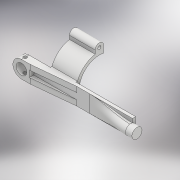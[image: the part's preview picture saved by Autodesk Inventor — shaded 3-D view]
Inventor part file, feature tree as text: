
AUTODESK INVENTOR PART (.ipt)
format: ipt  version: 2018 (Build 220112000, 112)  size: 248,320 bytes
history: native  units: mm
features: sketch x8, extrude x7, plane x3, projected_geometry x2, loft x1, mirror x1
ambient origin geometry x8: Origin, YZ Plane, XZ Plane, XY Plane, X Axis, Y Axis, Z Axis, Center Point
bodies: Solid1 (feature_tree)
feature tree (22):
  sketch  "Sketch1"  dims[d0=10.0mm d2=3.0mm]
  extrude  "Extrusion1"  Depth=3.0mm
  extrude  "Extrusion2"  Depth=16.0mm
  plane  "Work Plane1"
  extrude  "Extrusion3"  Depth=4.0mm TaperAngle=0.0deg
  sketch  "Sketch3"  dims[d5=3.0mm d6=0.0mm d7=4.0mm d8=0.0mm]
  plane  "Work Plane2"
  loft  "Loft1"
  extrude  "Extrusion4"  [1 undecoded]
  extrude  "Extrusion5"  Depth=10.0mm TaperAngle=90.0deg
  mirror  "Mirror1"
  extrude  "Extrusion6"  Depth=5.0mm TaperAngle=0.0deg
  plane  "Work Plane3"
  extrude  "Extrusion13"  Depth=24.0mm
  sketch  "Sketch2"  dims[d3=100.0mm d4=16.0mm]
  projected_geometry  "Projected Loop1"
  sketch  "Sketch4"  dims[d9=6.0mm d10=9.525mm]
  sketch  "Sketch6"  dims[d11=6.0mm d12=0.0mm d13=-40.0mm]
  sketch  "Sketch7"  dims[d14=10.0mm d15=90.0deg d16=10.0mm d17=90.0deg]
  projected_geometry  "Projected Loop2"
  sketch  "Sketch8"  dims[d20=40.0mm d21=5.0mm d22=0.0mm]
  sketch  "Sketch15"  dims[d23=5.0mm d24=0.0mm d25=3.2mm d26=5.0mm d27=0.0mm d75=20.0mm d76=38.5mm d77=3.0mm d78=3.0mm d79=50.0mm d80=22.0mm d81=25.0mm d82=4.0mm d83=22.0mm d84=24.0mm d85=0.0mm]
note: 1 required parameter value undecoded (feature->parameter linkage not recoverable at this tier; creation-order binding heuristic only, values carry confidence <= 0.55)
